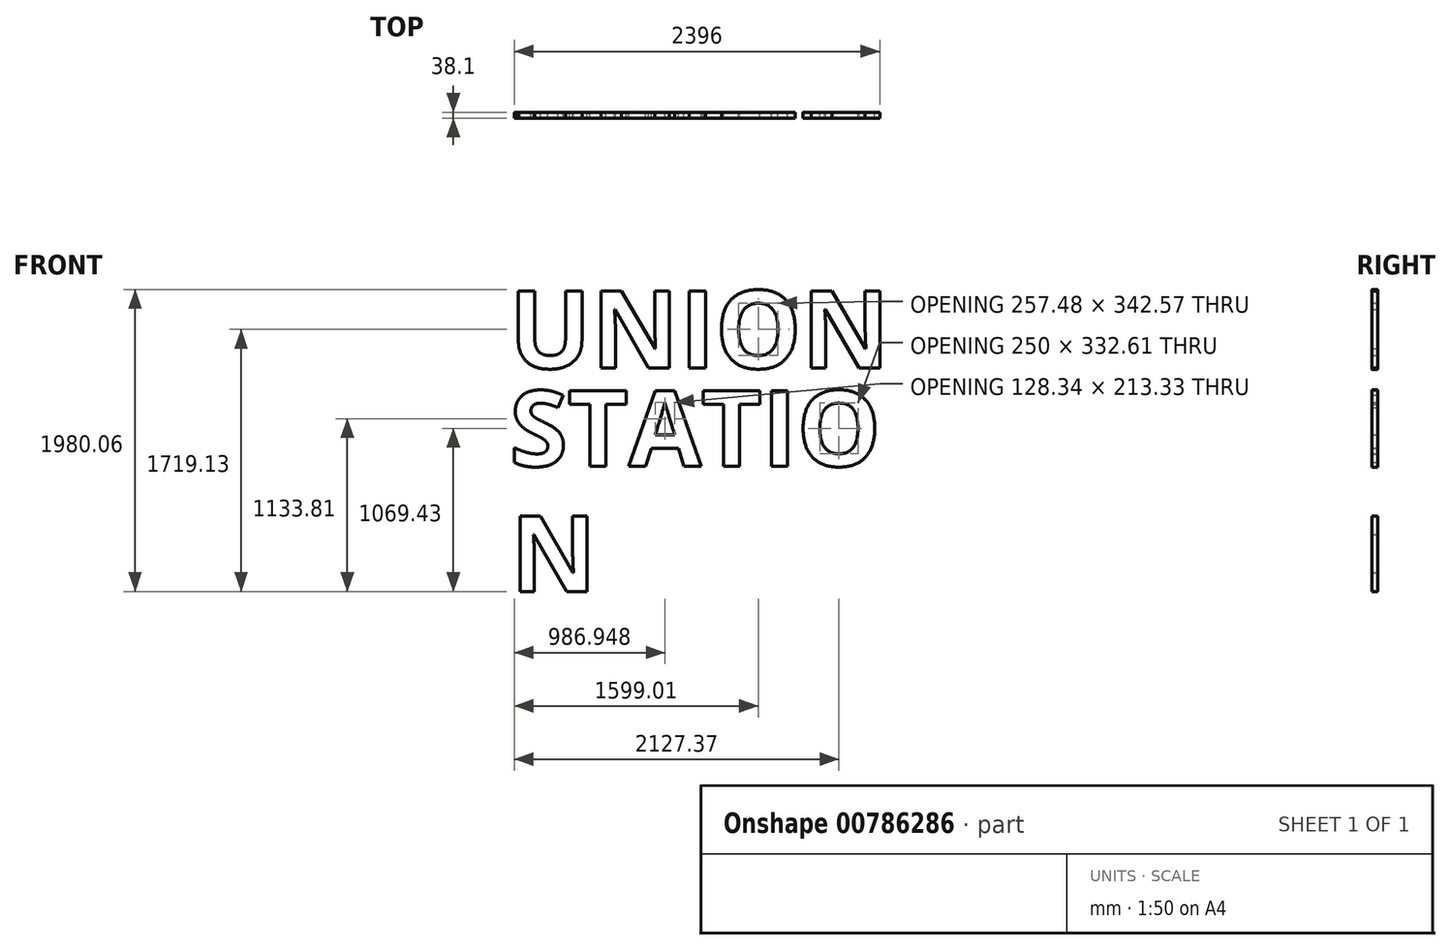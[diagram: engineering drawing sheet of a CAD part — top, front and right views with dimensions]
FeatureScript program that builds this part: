
annotation { "Feature Type Name" : "Feature", "Feature Type Description" : "" }
export const myFeature = defineFeature(function(context is Context, id is Id, definition is map)
    precondition{}
    {
        {
            var Q0;
            Q0=qCreatedBy(makeId("Front.planeOp"),FACE);
            var sketch = newSketch(context, id + "F0", { "sketchPlane" : qUnion([Q0])});
            skLineSegment(sketch, "E0.bottom", {"start": v(-1219.2, 304.8) * mm, "end": v(1219.2, 304.8) * mm});
            skLineSegment(sketch, "E0.top", {"start": v(-1219.2, -304.8) * mm, "end": v(1219.2, -304.8) * mm});
            skLineSegment(sketch, "E0.left", {"start": v(-1219.2, 304.8) * mm, "end": v(-1219.2, -304.8) * mm});
            skLineSegment(sketch, "E0.right", {"start": v(1219.2, 304.8) * mm, "end": v(1219.2, -304.8) * mm});
            skPoint(sketch, "E0.middle", {"position": v(0, 0) * mm});
            skText(sketch, "E1", { "text": "UNION", "fontName": "OpenSans-Bold.ttf"});
            skLineSegment(sketch, "E2.bottom", {"start": v(-1216.29, -340.3) * mm, "end": v(1222.11, -340.3) * mm});
            skLineSegment(sketch, "E2.top", {"start": v(-1216.29, -949.9) * mm, "end": v(1222.11, -949.9) * mm});
            skLineSegment(sketch, "E2.left", {"start": v(-1216.29, -340.3) * mm, "end": v(-1216.29, -949.9) * mm});
            skLineSegment(sketch, "E2.right", {"start": v(1222.11, -340.3) * mm, "end": v(1222.11, -949.9) * mm});
            skText(sketch, "E3", { "text": "STATIO", "fontName": "OpenSans-Bold.ttf"});
            skLineSegment(sketch, "E4.bottom", {"start": v(-1209.45, -1153.53) * mm, "end": v(-494.46, -1153.53) * mm});
            skLineSegment(sketch, "E4.top", {"start": v(-1209.45, -1763.13) * mm, "end": v(-494.46, -1763.13) * mm});
            skLineSegment(sketch, "E4.left", {"start": v(-1209.45, -1153.53) * mm, "end": v(-1209.45, -1763.13) * mm});
            skLineSegment(sketch, "E4.right", {"start": v(-494.46, -1153.53) * mm, "end": v(-494.46, -1763.13) * mm});
            skText(sketch, "E5", { "text": "N ", "fontName": "OpenSans-Bold.ttf"});
            const initialGuessF0  = {"E1": [-1.2192, -0.24612, 1, 0, 0.51185], "E3": [-1.21629, -0.88843, 1, 0, 0.49698], "E5": [-1.20945, -1.71066, 1, 0, 0.49852]};
            skSetInitialGuess(sketch, initialGuessF0);
            skSolve(sketch);
        }
        {
            var Q0;
            Q0=makeQuery(id+"F0.imprint","IMPRINT",FACE,{"disambiguationData":[TD([[makeQuery(id+"F0.imprint","IMPRINT",EDGE,{"derivedFrom":sQuery(id+"F0.wireOp",EDGE,"E1.sketch_text.stroke-0")}),-1.0]])]});
            var Q1;
            Q1=makeQuery(id+"F0.imprint","IMPRINT",FACE,{"disambiguationData":[TD([[makeQuery(id+"F0.imprint","IMPRINT",EDGE,{"derivedFrom":sQuery(id+"F0.wireOp",EDGE,"E1.sketch_text.stroke-15")}),-1.0]])]});
            var Q2;
            Q2=makeQuery(id+"F0.imprint","IMPRINT",FACE,{"disambiguationData":[TD([[makeQuery(id+"F0.imprint","IMPRINT",EDGE,{"derivedFrom":sQuery(id+"F0.wireOp",EDGE,"E1.sketch_text.stroke-29")}),-1.0]])]});
            var Q3;
            Q3=makeQuery(id+"F0.imprint","IMPRINT",FACE,{"disambiguationData":[TD([[makeQuery(id+"F0.imprint","IMPRINT",EDGE,{"derivedFrom":sQuery(id+"F0.wireOp",EDGE,"E1.sketch_text.stroke-33")}),-1.0]])]});
            var Q4;
            Q4=makeQuery(id+"F0.imprint","IMPRINT",FACE,{"disambiguationData":[TD([[makeQuery(id+"F0.imprint","IMPRINT",EDGE,{"derivedFrom":sQuery(id+"F0.wireOp",EDGE,"E1.sketch_text.stroke-47")}),-1.0]])]});
            extrude(context, id + "F1", {"entities" : qUnion([Q0, Q1, Q2, Q3, Q4]), "depth" : 38.1 * mm, "offsetDistance" : 25.4 * mm});
        }
        {
            var Q0;
            Q0=makeQuery(id+"F0.imprint","IMPRINT",FACE,{"disambiguationData":[TD([[makeQuery(id+"F0.imprint","IMPRINT",EDGE,{"derivedFrom":sQuery(id+"F0.wireOp",EDGE,"E3.sketch_text.stroke-0")}),-1.0]])]});
            var Q1;
            Q1=makeQuery(id+"F0.imprint","IMPRINT",FACE,{"disambiguationData":[TD([[makeQuery(id+"F0.imprint","IMPRINT",EDGE,{"derivedFrom":sQuery(id+"F0.wireOp",EDGE,"E3.sketch_text.stroke-28")}),-1.0]])]});
            var Q2;
            Q2=makeQuery(id+"F0.imprint","IMPRINT",FACE,{"disambiguationData":[TD([[makeQuery(id+"F0.imprint","IMPRINT",EDGE,{"derivedFrom":sQuery(id+"F0.wireOp",EDGE,"E3.sketch_text.stroke-36")}),-1.0]])]});
            var Q3;
            Q3=makeQuery(id+"F0.imprint","IMPRINT",FACE,{"disambiguationData":[TD([[makeQuery(id+"F0.imprint","IMPRINT",EDGE,{"derivedFrom":sQuery(id+"F0.wireOp",EDGE,"E3.sketch_text.stroke-48")}),-1.0]])]});
            var Q4;
            Q4=makeQuery(id+"F0.imprint","IMPRINT",FACE,{"disambiguationData":[TD([[makeQuery(id+"F0.imprint","IMPRINT",EDGE,{"derivedFrom":sQuery(id+"F0.wireOp",EDGE,"E3.sketch_text.stroke-56")}),-1.0]])]});
            var Q5;
            Q5=makeQuery(id+"F0.imprint","IMPRINT",FACE,{"disambiguationData":[TD([[makeQuery(id+"F0.imprint","IMPRINT",EDGE,{"derivedFrom":sQuery(id+"F0.wireOp",EDGE,"E3.sketch_text.stroke-60")}),-1.0]])]});
            extrude(context, id + "F2", {"entities" : qUnion([Q0, Q1, Q2, Q3, Q4, Q5]), "depth" : 38.1 * mm, "offsetDistance" : 25.4 * mm});
        }
        {
            var Q0;
            Q0=makeQuery(id+"F0.imprint","IMPRINT",FACE,{"disambiguationData":[TD([[makeQuery(id+"F0.imprint","IMPRINT",EDGE,{"derivedFrom":sQuery(id+"F0.wireOp",EDGE,"E5.sketch_text.stroke-0")}),-1.0]])]});
            extrude(context, id + "F3", {"entities" : qUnion([Q0]), "depth" : 38.1 * mm, "offsetDistance" : 25.4 * mm});
        }
    });
